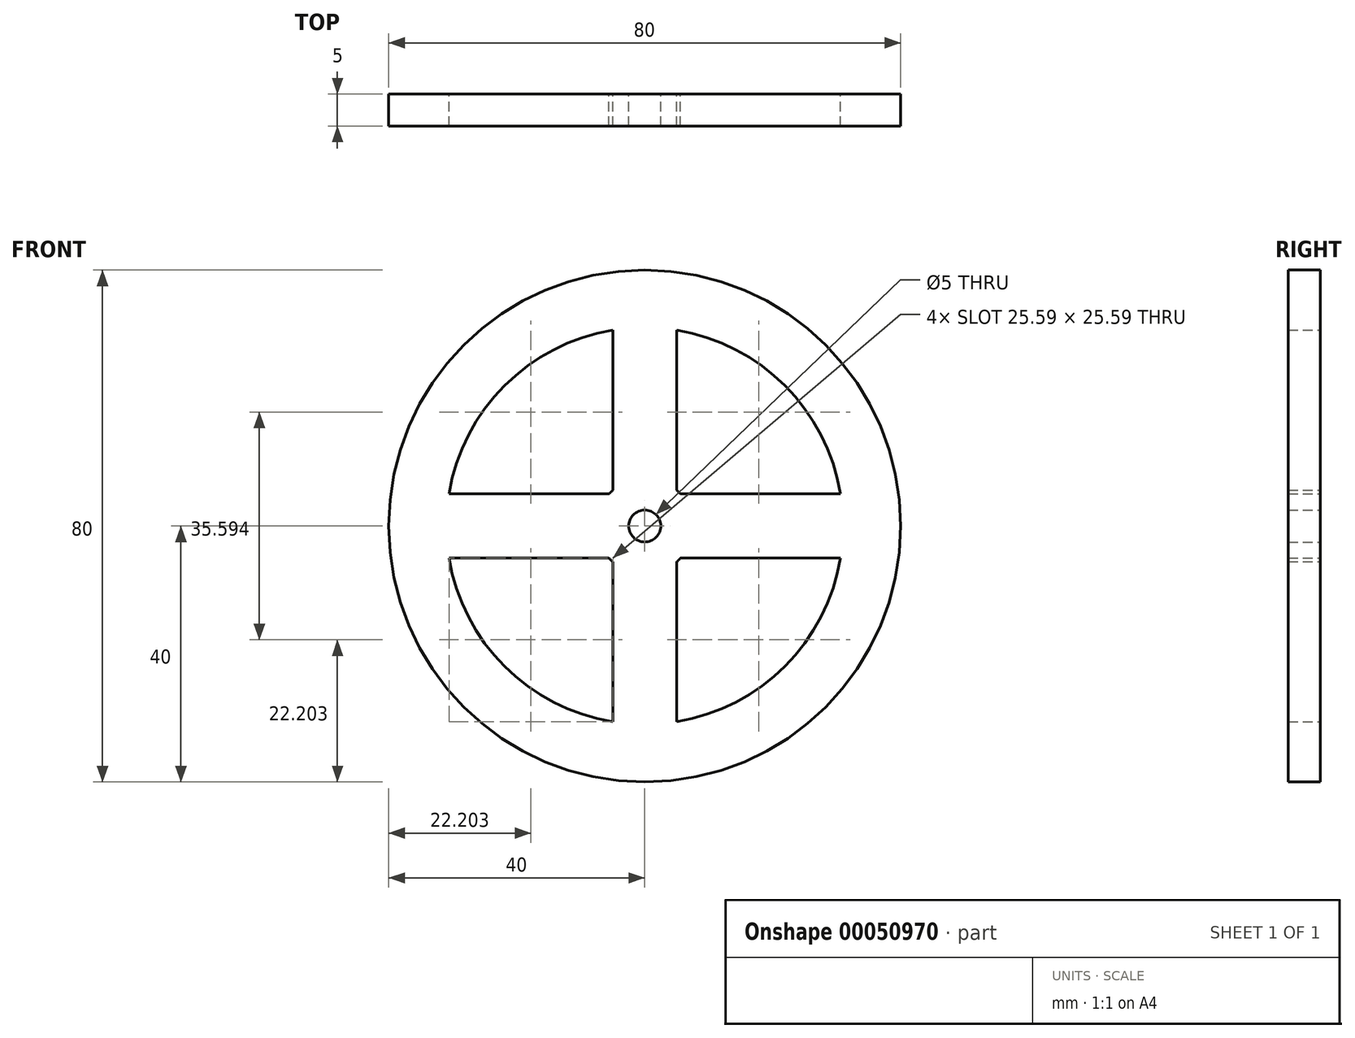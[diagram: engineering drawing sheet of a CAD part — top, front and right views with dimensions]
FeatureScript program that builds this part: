
annotation { "Feature Type Name" : "Feature", "Feature Type Description" : "" }
export const myFeature = defineFeature(function(context is Context, id is Id, definition is map)
    precondition{}
    {
        {
            var Q0;
            Q0=qCreatedBy(makeId("Front.planeOp"),FACE);
            var sketch = newSketch(context, id + "F0", { "sketchPlane" : qUnion([Q0])});
            skCircle(sketch, "E0", {"center": v(0, 0) * mm, "radius": 40 * mm});
            skArc(sketch, "E1", {"start": v(-30.6, -5) * mm, "mid": v(-21.92, -21.92) * mm, "end": v(-5, -30.6) * mm});
            skArc(sketch, "E2", {"start": v(-5.6, -5) * mm, "mid": v(-5.3, -5.3) * mm, "end": v(-5, -5.6) * mm});
            skCircle(sketch, "E3", {"center": v(0, 0) * mm, "radius": 2.5 * mm});
            skLineSegment(sketch, "E4.0", {"start": v(5.6, -5) * mm, "end": v(30.6, -5) * mm});
            skLineSegment(sketch, "E5.0", {"start": v(5.6, 5) * mm, "end": v(30.6, 5) * mm});
            skLineSegment(sketch, "E6.0", {"start": v(-5, -5.6) * mm, "end": v(-5, -30.6) * mm});
            skLineSegment(sketch, "E7.0", {"start": v(5, -5.6) * mm, "end": v(5, -30.6) * mm});
            skLineSegment(sketch, "E8.0", {"start": v(-5.6, -5) * mm, "end": v(-30.6, -5) * mm});
            skPoint(sketch, "E9.orphan", {"position": v(0, 40) * mm});
            skLineSegment(sketch, "E10.trimOffspring", {"start": v(-5.6, 5) * mm, "end": v(-30.6, 5) * mm});
            skLineSegment(sketch, "E11.trimOffspring", {"start": v(-5, 5.6) * mm, "end": v(-5, 30.6) * mm});
            skArc(sketch, "E12.trimOffspring", {"start": v(-5, 5.6) * mm, "mid": v(-5.3, 5.3) * mm, "end": v(-5.6, 5) * mm});
            skLineSegment(sketch, "E13.trimOffspring", {"start": v(5, 5.6) * mm, "end": v(5, 30.6) * mm});
            skArc(sketch, "E14.trimOffspring", {"start": v(5, -5.6) * mm, "mid": v(5.3, -5.3) * mm, "end": v(5.6, -5) * mm});
            skArc(sketch, "E15.trimOffspring", {"start": v(5.6, 5) * mm, "mid": v(5.3, 5.3) * mm, "end": v(5, 5.6) * mm});
            skArc(sketch, "E16.trimOffspring", {"start": v(5, -30.6) * mm, "mid": v(21.92, -21.92) * mm, "end": v(30.6, -5) * mm});
            skArc(sketch, "E17.trimOffspring", {"start": v(-5, 30.6) * mm, "mid": v(-21.92, 21.92) * mm, "end": v(-30.6, 5) * mm});
            skArc(sketch, "E18.trimOffspring", {"start": v(30.6, 5) * mm, "mid": v(21.92, 21.92) * mm, "end": v(5, 30.6) * mm});
            skSolve(sketch);
        }
        {
            var Q0;
            Q0=makeQuery(id+"F0.imprint","IMPRINT",FACE,{"disambiguationData":[TD([[makeQuery(id+"F0.imprint","IMPRINT",EDGE,{"derivedFrom":sQuery(id+"F0.wireOp",EDGE,"E0")}),1.0]])]});
            extrude(context, id + "F1", {"entities" : qUnion([Q0]), "depth" : 5 * mm});
        }
    });
